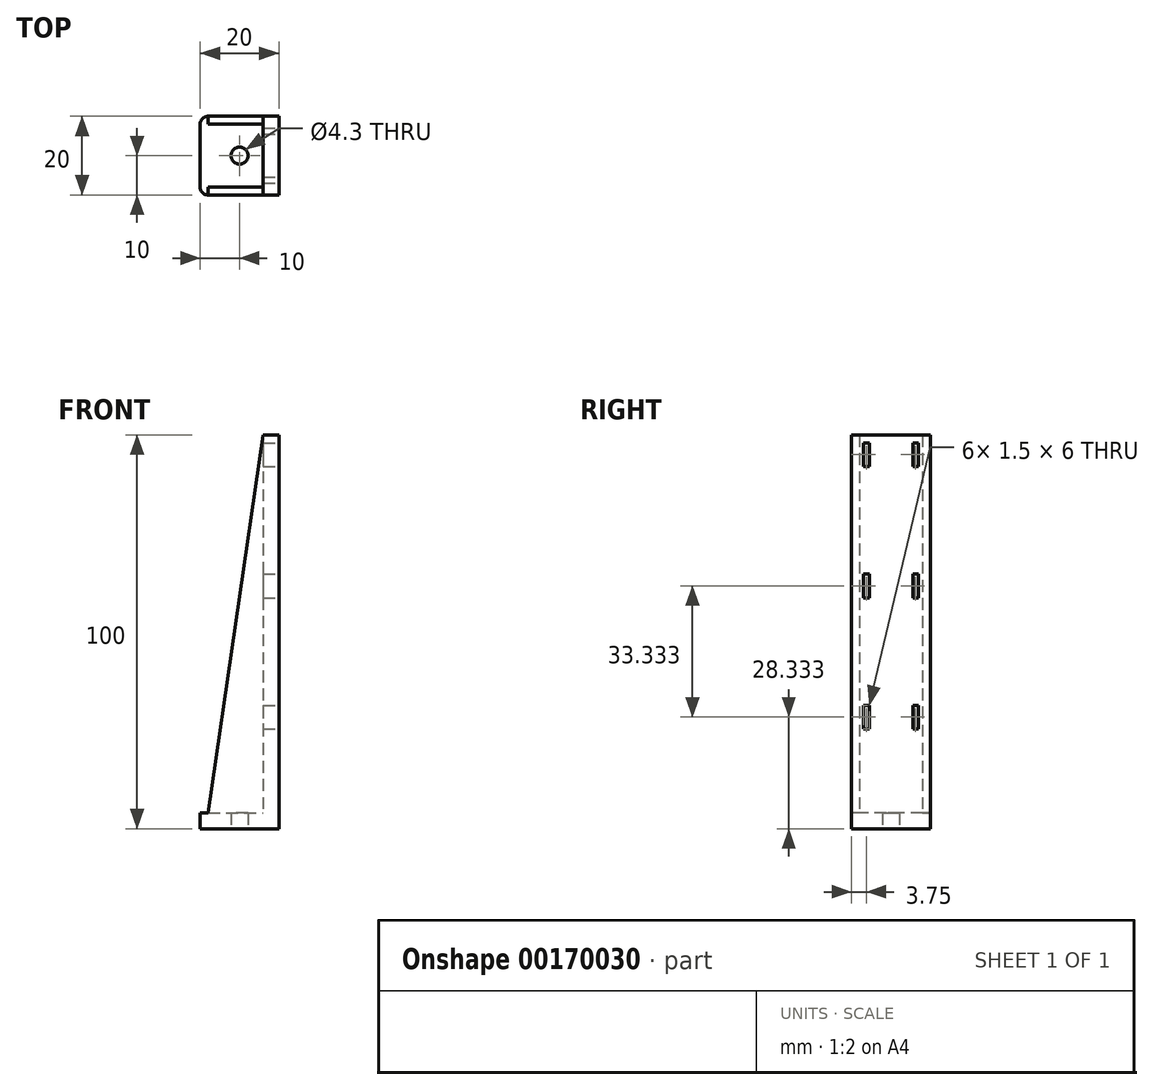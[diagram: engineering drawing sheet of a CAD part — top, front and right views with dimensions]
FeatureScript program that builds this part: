
annotation { "Feature Type Name" : "Feature", "Feature Type Description" : "" }
export const myFeature = defineFeature(function(context is Context, id is Id, definition is map)
    precondition{}
    {
        {
            var Q0;
            Q0=qCreatedBy(makeId("Top.planeOp"),FACE);
            var sketch = newSketch(context, id + "F0", { "sketchPlane" : qUnion([Q0])});
            skLineSegment(sketch, "E0.bottom", {"start": v(0, 0) * mm, "end": v(20, 0) * mm});
            skLineSegment(sketch, "E0.top", {"start": v(0, 20) * mm, "end": v(20, 20) * mm});
            skLineSegment(sketch, "E0.left", {"start": v(0, 0) * mm, "end": v(0, 20) * mm});
            skLineSegment(sketch, "E0.right", {"start": v(20, 0) * mm, "end": v(20, 20) * mm});
            skCircle(sketch, "E1", {"center": v(10, 10) * mm, "radius": 2.15 * mm});
            skPoint(sketch, "E1.centerSnap0", {"position": v(20, 10) * mm});
            skPoint(sketch, "E1.centerSnap1", {"position": v(10, 20) * mm});
            skSolve(sketch);
        }
        {
            var Q0;
            Q0=makeQuery(id+"F0.imprint","IMPRINT",FACE,{"disambiguationData":[TD([[makeQuery(id+"F0.imprint","IMPRINT",EDGE,{"derivedFrom":sQuery(id+"F0.wireOp",EDGE,"E0.bottom")}),1.0]])]});
            extrude(context, id + "F1", {"entities" : qUnion([Q0]), "depth" : 4 * mm});
        }
        {
            var Q0;
            Q0=makeQuery(id+"F1.opExtrude","CAP_FACE",FACE,{"disambiguationData":[OSD([sQuery(id+"F0.wireOp",EDGE,"E0.bottom"),sQuery(id+"F0.wireOp",EDGE,"E0.top"),sQuery(id+"F0.wireOp",EDGE,"E0.left"),sQuery(id+"F0.wireOp",EDGE,"E0.right"),sQuery(id+"F0.wireOp",EDGE,"E1")])],"isStart":false});
            var sketch = newSketch(context, id + "F2", { "sketchPlane" : qUnion([Q0])});
            skLineSegment(sketch, "E2.bottom", {"start": v(20, 20) * mm, "end": v(16, 20) * mm});
            skLineSegment(sketch, "E2.top", {"start": v(20, 0) * mm, "end": v(16, 0) * mm});
            skLineSegment(sketch, "E2.left", {"start": v(20, 20) * mm, "end": v(20, 0) * mm});
            skLineSegment(sketch, "E2.right", {"start": v(16, 20) * mm, "end": v(16, 0) * mm});
            skSolve(sketch);
        }
        {
            var Q0;
            Q0=makeQuery(id+"F2.imprint","IMPRINT",FACE,{"disambiguationData":[TD([[makeQuery(id+"F2.imprint","IMPRINT",EDGE,{"derivedFrom":sQuery(id+"F2.wireOp",EDGE,"E2.bottom")}),-1.0]])]});
            extrude(context, id + "F3", {"entities" : qUnion([Q0]), "operationType" : NewBodyOperationType.ADD, "depth" : (100 - 4) * mm});
        }
        {
            var Q0;
            Q0=makeQuery(id+"F3.boolean.opBoolean","MERGE",FACE,{"derivedFrom":[makeQuery(id+"F1.opExtrude","SWEPT_FACE",FACE,{"disambiguationData":[OSD([sQuery(id+"F0.wireOp",EDGE,"E0.right")])]}),makeQuery(id+"F3.opExtrude","SWEPT_FACE",FACE,{"disambiguationData":[OSD([sQuery(id+"F2.wireOp",EDGE,"E2.left")])]})]});
            var sketch = newSketch(context, id + "F4", { "sketchPlane" : qUnion([Q0])});
            skLineSegment(sketch, "E3.bottom", {"start": v(3, 98) * mm, "end": v(4.5, 98) * mm});
            skLineSegment(sketch, "E3.top", {"start": v(3, 92) * mm, "end": v(4.5, 92) * mm});
            skLineSegment(sketch, "E3.left", {"start": v(3, 98) * mm, "end": v(3, 92) * mm});
            skLineSegment(sketch, "E3.right", {"start": v(4.5, 98) * mm, "end": v(4.5, 92) * mm});
            skLineSegment(sketch, "E4.bottom", {"start": v(15.5, 98) * mm, "end": v(17, 98) * mm});
            skLineSegment(sketch, "E4.top", {"start": v(15.5, 92) * mm, "end": v(17, 92) * mm});
            skLineSegment(sketch, "E4.left", {"start": v(15.5, 98) * mm, "end": v(15.5, 92) * mm});
            skLineSegment(sketch, "E4.right", {"start": v(17, 98) * mm, "end": v(17, 92) * mm});
            skLineSegment(sketch, "E5.1.0.0", {"start": v(3, 64.67) * mm, "end": v(4.5, 64.67) * mm});
            skLineSegment(sketch, "E5.1.0.1", {"start": v(3, 64.67) * mm, "end": v(3, 58.67) * mm});
            skLineSegment(sketch, "E5.1.0.2", {"start": v(3, 58.67) * mm, "end": v(4.5, 58.67) * mm});
            skLineSegment(sketch, "E5.1.0.3", {"start": v(4.5, 64.67) * mm, "end": v(4.5, 58.67) * mm});
            skLineSegment(sketch, "E5.1.0.4", {"start": v(15.5, 58.67) * mm, "end": v(17, 58.67) * mm});
            skLineSegment(sketch, "E5.1.0.5", {"start": v(15.5, 64.67) * mm, "end": v(15.5, 58.67) * mm});
            skLineSegment(sketch, "E5.1.0.6", {"start": v(17, 64.67) * mm, "end": v(17, 58.67) * mm});
            skLineSegment(sketch, "E5.1.0.7", {"start": v(15.5, 64.67) * mm, "end": v(17, 64.67) * mm});
            skLineSegment(sketch, "E5.2.0.0", {"start": v(3, 31.33) * mm, "end": v(4.5, 31.33) * mm});
            skLineSegment(sketch, "E5.2.0.1", {"start": v(3, 31.33) * mm, "end": v(3, 25.33) * mm});
            skLineSegment(sketch, "E5.2.0.2", {"start": v(3, 25.33) * mm, "end": v(4.5, 25.33) * mm});
            skLineSegment(sketch, "E5.2.0.3", {"start": v(4.5, 31.33) * mm, "end": v(4.5, 25.33) * mm});
            skLineSegment(sketch, "E5.2.0.4", {"start": v(15.5, 25.33) * mm, "end": v(17, 25.33) * mm});
            skLineSegment(sketch, "E5.2.0.5", {"start": v(15.5, 31.33) * mm, "end": v(15.5, 25.33) * mm});
            skLineSegment(sketch, "E5.2.0.6", {"start": v(17, 31.33) * mm, "end": v(17, 25.33) * mm});
            skLineSegment(sketch, "E5.2.0.7", {"start": v(15.5, 31.33) * mm, "end": v(17, 31.33) * mm});
            skLineSegment(sketch, "E5.direction1", {"start": v(3, 92) * mm, "end": v(3, 58.67) * mm, "construction": true});
            skSolve(sketch);
        }
        {
            var Q0;
            Q0 = qSketchRegion(id + "F4", true);
            extrude(context, id + "F5", {"entities" : qUnion([Q0]), "operationType" : NewBodyOperationType.REMOVE, "endBound" : BoundingType.THROUGH_ALL, "oppositeDirection" : true, "depth" : 25 * mm});
        }
        {
            var Q0;
            Q0=makeQuery(id+"F1.opExtrude","SWEPT_EDGE",EDGE,{"disambiguationData":[OSD([sQuery(id+"F0.wireOp",EDGE,"E0.bottom"),sQuery(id+"F0.wireOp",EDGE,"E0.left")])]});
            var Q1;
            Q1=makeQuery(id+"F1.opExtrude","SWEPT_EDGE",EDGE,{"disambiguationData":[OSD([sQuery(id+"F0.wireOp",EDGE,"E0.top"),sQuery(id+"F0.wireOp",EDGE,"E0.left")])]});
            fillet(context, id + "F6", {"entities" : qUnion([Q0, Q1]), "radius" : 2 * mm, "tangentPropagation" : true, "allowEdgeOverflow" : false});
        }
        {
            var Q0;
            Q0=makeQuery(id+"F3.boolean.opBoolean","MERGE",FACE,{"derivedFrom":[makeQuery(id+"F1.opExtrude","SWEPT_FACE",FACE,{"disambiguationData":[OSD([sQuery(id+"F0.wireOp",EDGE,"E0.bottom")])]}),makeQuery(id+"F3.opExtrude","SWEPT_FACE",FACE,{"disambiguationData":[OSD([sQuery(id+"F2.wireOp",EDGE,"E2.top")])]})]});
            var sketch = newSketch(context, id + "F7", { "sketchPlane" : qUnion([Q0])});
            skLineSegment(sketch, "E6", {"start": v(16, 100) * mm, "end": v(2, 4) * mm});
            skSolve(sketch);
        }
        {
            var Q0;
            Q0=makeQuery(id+"F7.imprint","IMPRINT",FACE,{"disambiguationData":[TD([[makeQuery(id+"F7.imprint","IMPRINT",EDGE,{"derivedFrom":sQuery(id+"F7.wireOp",EDGE,"E6")}),1.0]])]});
            extrude(context, id + "F8", {"entities" : qUnion([Q0]), "operationType" : NewBodyOperationType.ADD, "oppositeDirection" : true, "depth" : 2 * mm});
        }
        {
            var Q0;
            Q0=makeQuery(id+"F3.boolean.opBoolean","MERGE",FACE,{"derivedFrom":[makeQuery(id+"F1.opExtrude","SWEPT_FACE",FACE,{"disambiguationData":[OSD([sQuery(id+"F0.wireOp",EDGE,"E0.top")])]}),makeQuery(id+"F3.opExtrude","SWEPT_FACE",FACE,{"disambiguationData":[OSD([sQuery(id+"F2.wireOp",EDGE,"E2.bottom")])]})]});
            var sketch = newSketch(context, id + "F9", { "sketchPlane" : qUnion([Q0])});
            skLineSegment(sketch, "E7", {"start": v(-2, 4) * mm, "end": v(-16, 100) * mm});
            skSolve(sketch);
        }
        {
            var Q0;
            Q0=makeQuery(id+"F9.imprint","IMPRINT",FACE,{"disambiguationData":[TD([[makeQuery(id+"F9.imprint","IMPRINT",EDGE,{"derivedFrom":sQuery(id+"F9.wireOp",EDGE,"E7")}),1.0]])]});
            extrude(context, id + "F10", {"entities" : qUnion([Q0]), "operationType" : NewBodyOperationType.ADD, "oppositeDirection" : true, "depth" : 2 * mm});
        }
    });
